# Revit family: NXOFM_On-Fixture_Module
name_source: partatom
category: Communication Devices
revit_build: Autodesk Revit 2014 (Build: 20130308_1515(x64)
units: mm (PartAtom-declared; Revit-internal decimal feet)

## types (1)
- NXOFM_On-Fixture_Module
    Assembly Code = D5090
    Certifications = Conforms with UL916 and Certified to CAN/CSA C22.2 No. 205-M1983
IC Approved
FCC ID: YH9NXOFM1R1DUNV IC: 9044A-NXOFM1R1DUNV
Contains FCC ID: U9O-SM220 IC: 7084A-SM22
    Default Elevation = 48 "
    Description = The On-Fixture Module incorporates a single pole relay for On/Off control as well as industry standard 0 - 10 volt continuous dimming control.
    Electrical Rating = Input: 120-480VAC, 16A Max, 50-60Hz
Output: 5A@120-347V, 3A@480V
Surge Withstand: 2000V
Peak Inrush: 160A for 2 ms Max
Standby Power (W):
120VAC: 1.2
277VAC: 1.5
347VAC: 1.5
480VAC:1.3
    Housing Material = Paint - Hubbell - Carbon Black
    L = 5.26 "
    Manufacturer = Hubbell Control Solutions
    Model = NX On-Fixture Module
    Product Documentation Link = https://hubbellcdn.com
    Product Features = Designed for installation on the exterior of the luminaire housing
• NEMA standard male 7-pin twist lock connection
• Integral singe pole relay for On/Off control
• Continuous dimming 0 - 10V control
• Wireless programming via NX Area Controller or NX Room Setup App
for iOS or Android
• Power measurement
• Auxiliary input for external control
• UL and cUL listed
• Five year warranty
• Built-in daylight sensor
    Product Page URL = https://www.hubbell.com
    Type Comments = NX On-Fixture Module
    URL = https://www.hubbell.com
    Warranty = 5-Years Warranty

## geometry (parser evidence)
native form markers: Sweep x1
no freeform markers — native parametric forms only
